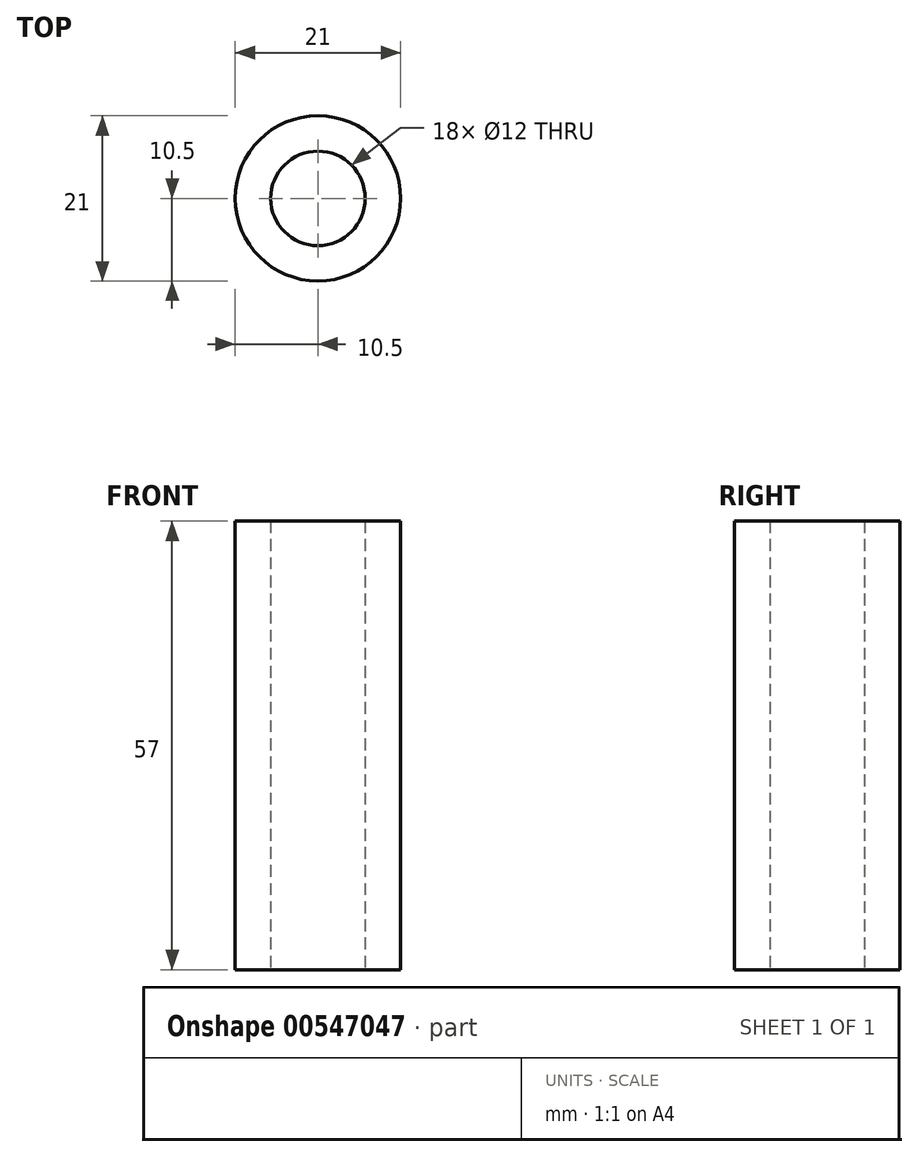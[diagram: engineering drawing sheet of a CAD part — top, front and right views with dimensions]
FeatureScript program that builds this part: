
annotation { "Feature Type Name" : "Feature", "Feature Type Description" : "" }
export const myFeature = defineFeature(function(context is Context, id is Id, definition is map)
    precondition{}
    {
        {
            var Q0;
            Q0=qCreatedBy(makeId("Top.planeOp"),FACE);
            var sketch = newSketch(context, id + "F0", { "sketchPlane" : qUnion([Q0])});
            skCircle(sketch, "E0", {"center": v(0, 0) * mm, "radius": 6 * mm});
            skCircle(sketch, "E1", {"center": v(0, 0) * mm, "radius": 10.5 * mm});
            skSolve(sketch);
        }
        {
            var Q0;
            Q0=makeQuery(id+"F0.imprint","IMPRINT",FACE,{"disambiguationData":[TD([[makeQuery(id+"F0.imprint","IMPRINT",EDGE,{"derivedFrom":sQuery(id+"F0.wireOp",EDGE,"E0")}),-1.0]])]});
            extrude(context, id + "F1", {"entities" : qUnion([Q0]), "depth" : 57 * mm, "offsetDistance" : 25 * mm});
        }
    });
